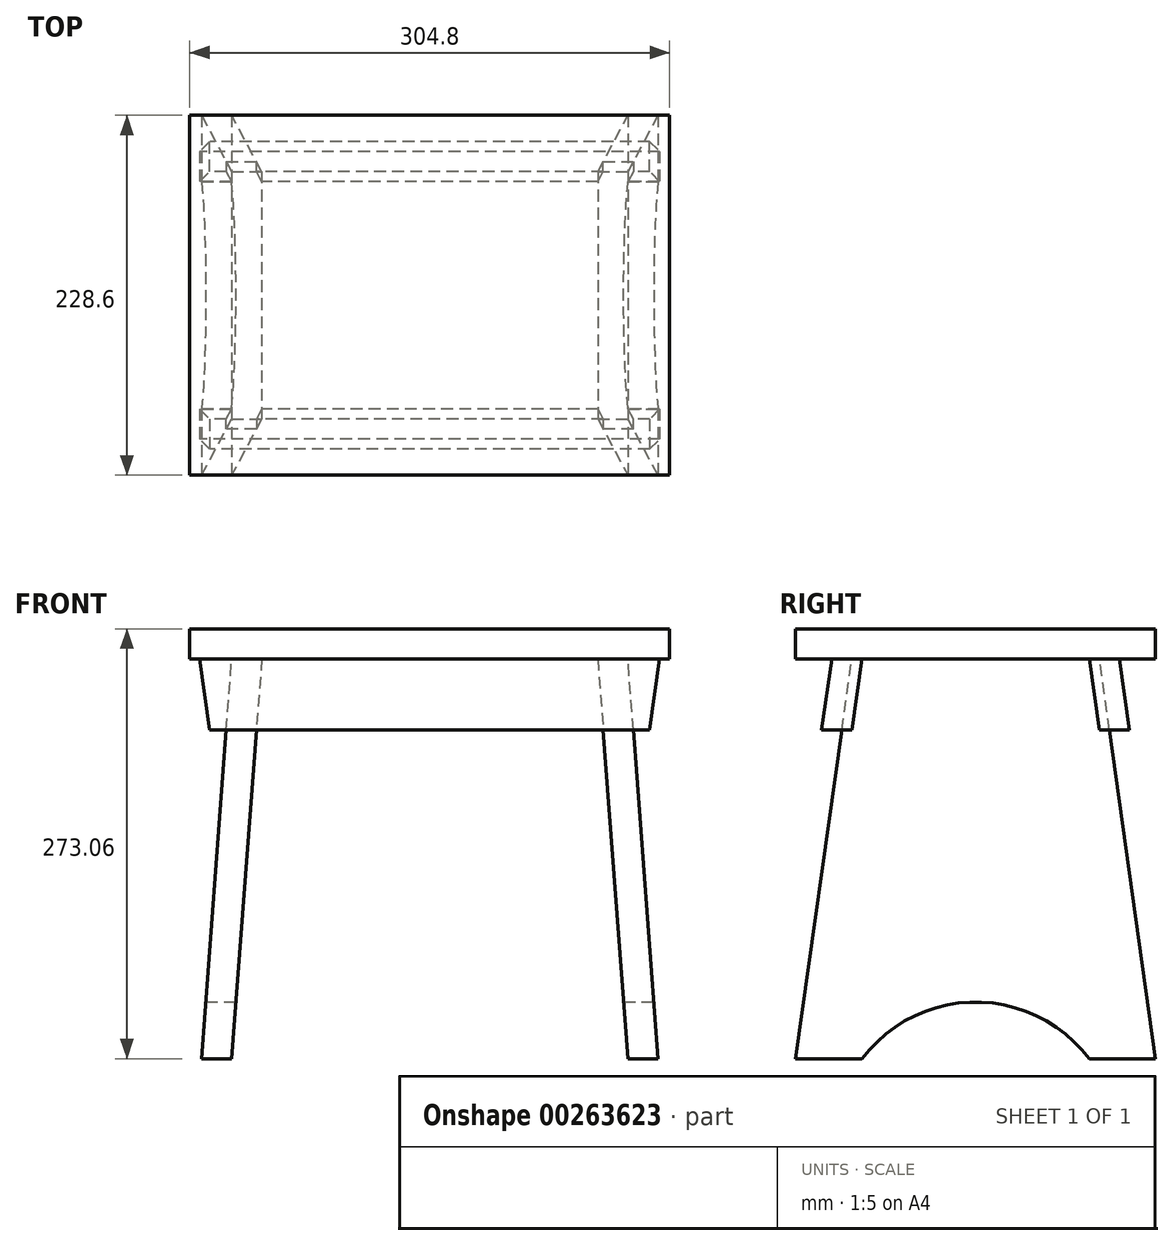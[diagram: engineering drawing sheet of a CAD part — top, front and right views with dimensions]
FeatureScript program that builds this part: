
annotation { "Feature Type Name" : "Feature", "Feature Type Description" : "" }
export const myFeature = defineFeature(function(context is Context, id is Id, definition is map)
    precondition{}
    {
        {
            var Q0;
            Q0=qCreatedBy(makeId("Front.planeOp"),FACE);
            var sketch = newSketch(context, id + "F0", { "sketchPlane" : qUnion([Q0])});
            skLineSegment(sketch, "E0.bottom", {"start": v(152.4, 9.52) * mm, "end": v(-152.4, 9.52) * mm});
            skLineSegment(sketch, "E0.top", {"start": v(152.4, -9.53) * mm, "end": v(-152.4, -9.53) * mm});
            skLineSegment(sketch, "E0.left", {"start": v(152.4, 9.52) * mm, "end": v(152.4, -9.52) * mm});
            skLineSegment(sketch, "E0.right", {"start": v(-152.4, 9.52) * mm, "end": v(-152.4, -9.53) * mm});
            skPoint(sketch, "E0.middle", {"position": v(0, 0) * mm});
            skLineSegment(sketch, "E1.bottom", {"start": v(-152.4, -9.53) * mm, "end": v(152.4, -9.53) * mm, "construction": true});
            skLineSegment(sketch, "E1.top", {"start": v(-152.4, -263.53) * mm, "end": v(152.4, -263.53) * mm, "construction": true});
            skLineSegment(sketch, "E1.left", {"start": v(-152.4, -9.52) * mm, "end": v(-152.4, -263.53) * mm, "construction": true});
            skLineSegment(sketch, "E1.right", {"start": v(152.4, -9.52) * mm, "end": v(152.4, -263.52) * mm, "construction": true});
            skLineSegment(sketch, "E2", {"start": v(106.74, -9.53) * mm, "end": v(125.85, -263.53) * mm});
            skLineSegment(sketch, "E3", {"start": v(125.85, -263.53) * mm, "end": v(144.95, -263.53) * mm});
            skLineSegment(sketch, "E4", {"start": v(144.95, -263.52) * mm, "end": v(125.85, -9.52) * mm});
            skLineSegment(sketch, "E5", {"start": v(125.85, -9.52) * mm, "end": v(106.74, -9.53) * mm});
            skLineSegment(sketch, "E6", {"start": v(0, -9.52) * mm, "end": v(0, -263.53) * mm, "construction": true});
            skLineSegment(sketch, "E7.MirrorCS", {"start": v(-144.95, -263.53) * mm, "end": v(-125.85, -9.52) * mm});
            skLineSegment(sketch, "E8.MirrorCS", {"start": v(-106.74, -9.52) * mm, "end": v(-125.85, -263.53) * mm});
            skLineSegment(sketch, "E9.MirrorCS", {"start": v(-125.85, -263.53) * mm, "end": v(-144.95, -263.53) * mm});
            skLineSegment(sketch, "E10.MirrorCS", {"start": v(-125.85, -9.52) * mm, "end": v(-106.74, -9.53) * mm});
            skLineSegment(sketch, "E11.bottom", {"start": v(-152.4, -9.53) * mm, "end": v(152.4, -9.53) * mm});
            skLineSegment(sketch, "E11.top", {"start": v(-152.4, -63.28) * mm, "end": v(152.4, -63.28) * mm});
            skLineSegment(sketch, "E11.left", {"start": v(-152.4, -9.53) * mm, "end": v(-152.4, -63.28) * mm});
            skLineSegment(sketch, "E11.right", {"start": v(152.4, -9.53) * mm, "end": v(152.4, -63.28) * mm});
            skLineSegment(sketch, "E12", {"start": v(146.05, -9.52) * mm, "end": v(138.5, -63.28) * mm});
            skLineSegment(sketch, "E13.MirrorCS", {"start": v(-146.05, -9.53) * mm, "end": v(-138.5, -63.28) * mm});
            skSolve(sketch);
        }
        {
            var Q0;
            Q0=makeQuery(id+"F0.imprint","IMPRINT",FACE,{"disambiguationData":[TD([[makeQuery(id+"F0.imprint","IMPRINT",EDGE,{"derivedFrom":sQuery(id+"F0.wireOp",EDGE,"E0.bottom")}),1.0]])]});
            extrude(context, id + "F1", {"entities" : qUnion([Q0]), "endBound" : BoundingType.SYMMETRIC, "depth" : 228.6 * mm});
        }
        {
            var Q0;
            {var subQ0=sQuery(id+"F0.wireOp",EDGE,"E3");Q0=makeQuery(id+"F0.imprint","IMPRINT",FACE,{"disambiguationData":[TD([[makeQuery(id+"F0.imprint","IMPRINT",EDGE,{"derivedFrom":subQ0}),1.0]])]});}
            var Q1;
            {var subQ0=sQuery(id+"F0.wireOp",EDGE,"E11.bottom");var subQ1=sQuery(id+"F0.wireOp",EDGE,"E2");var subQ2=makeQuery(id+"F0.imprint","INTERSECT",VERTEX,{"derivedFrom":[subQ1,subQ0]});Q1=makeQuery(id+"F0.imprint","IMPRINT",FACE,{"disambiguationData":[TD([[makeQuery(id+"F0.imprint","IMPRINT",EDGE,{"disambiguationData":[TD([[subQ2,-1.0]])],"derivedFrom":subQ1}),1.0]])]});}
            var Q2;
            {var subQ0=sQuery(id+"F0.wireOp",EDGE,"E11.bottom");var subQ1=sQuery(id+"F0.wireOp",EDGE,"E7.MirrorCS");var subQ2=makeQuery(id+"F0.imprint","INTERSECT",VERTEX,{"derivedFrom":[subQ1,subQ0]});Q2=makeQuery(id+"F0.imprint","IMPRINT",FACE,{"disambiguationData":[TD([[makeQuery(id+"F0.imprint","IMPRINT",EDGE,{"disambiguationData":[TD([[subQ2,1.0]])],"derivedFrom":subQ1}),-1.0]])]});}
            var Q3;
            {var subQ0=sQuery(id+"F0.wireOp",EDGE,"E9.MirrorCS");Q3=makeQuery(id+"F0.imprint","IMPRINT",FACE,{"disambiguationData":[TD([[makeQuery(id+"F0.imprint","IMPRINT",EDGE,{"derivedFrom":subQ0}),-1.0]])]});}
            var Q4;
            Q4=makeQuery(id+"F1.opExtrude","CAP_VERTEX",VERTEX,{"disambiguationData":[OSD([sQuery(id+"F0.wireOp",EDGE,"E0.right"),sQuery(id+"F0.wireOp",EDGE,"E11.bottom"),sQuery(id+"F0.wireOp",EDGE,"E11.left")])],"isStart":true});
            var Q5;
            Q5=makeQuery(id+"F1.opExtrude","CAP_VERTEX",VERTEX,{"disambiguationData":[OSD([sQuery(id+"F0.wireOp",EDGE,"E0.right"),sQuery(id+"F0.wireOp",EDGE,"E11.bottom"),sQuery(id+"F0.wireOp",EDGE,"E11.left")])],"isStart":false});
            extrude(context, id + "F2", {"entities" : qUnion([Q0, Q1, Q2, Q3]), "endBound" : BoundingType.UP_TO_VERTEX, "oppositeDirection" : true, "endBoundEntityVertex" : qUnion([Q4]), "depth" : 25.4 * mm, "hasSecondDirection" : true, "secondDirectionBound" : SecondDirectionBoundingType.UP_TO_VERTEX, "secondDirectionOppositeDirection" : false, "secondDirectionBoundEntityVertex" : qUnion([Q5]), "secondDirectionDepth" : 25.4 * mm});
        }
        {
            var Q0;
            Q0=qCreatedBy(makeId("Right.planeOp"),FACE);
            var sketch = newSketch(context, id + "F3", { "sketchPlane" : qUnion([Q0])});
            skLineSegment(sketch, "E14.0.0", {"start": v(-114.3, -263.53) * mm, "end": v(114.3, -263.53) * mm});
            skLineSegment(sketch, "E14.0.1", {"start": v(114.3, -263.53) * mm, "end": v(114.3, -9.53) * mm});
            skLineSegment(sketch, "E14.0.2", {"start": v(114.3, -9.53) * mm, "end": v(-114.3, -9.53) * mm});
            skLineSegment(sketch, "E14.0.3", {"start": v(-114.3, -9.53) * mm, "end": v(-114.3, -263.53) * mm});
            skLineSegment(sketch, "E15", {"start": v(114.3, -263.53) * mm, "end": v(78.6, -9.52) * mm});
            skLineSegment(sketch, "E16.MirrorCS", {"start": v(-114.3, -263.53) * mm, "end": v(-78.6, -9.52) * mm});
            skArc(sketch, "E17", {"start": v(72.12, -263.53) * mm, "mid": v(0, -227.49) * mm, "end": v(-72.12, -263.53) * mm});
            skLineSegment(sketch, "E18", {"start": v(0, -317.67) * mm, "end": v(0, -263.53) * mm, "construction": true});
            skSolve(sketch);
        }
        {
            var Q0;
            {var subQ0=sQuery(id+"F3.wireOp",EDGE,"E14.0.1");Q0=makeQuery(id+"F3.imprint","IMPRINT",FACE,{"disambiguationData":[TD([[makeQuery(id+"F3.imprint","IMPRINT",EDGE,{"derivedFrom":subQ0}),1.0]])]});}
            var Q1;
            {var subQ0=sQuery(id+"F3.wireOp",EDGE,"E17");Q1=makeQuery(id+"F3.imprint","IMPRINT",FACE,{"disambiguationData":[TD([[makeQuery(id+"F3.imprint","IMPRINT",EDGE,{"derivedFrom":subQ0}),1.0]])]});}
            var Q2;
            {var subQ0=sQuery(id+"F3.wireOp",EDGE,"E14.0.3");Q2=makeQuery(id+"F3.imprint","IMPRINT",FACE,{"disambiguationData":[TD([[makeQuery(id+"F3.imprint","IMPRINT",EDGE,{"derivedFrom":subQ0}),1.0]])]});}
            extrude(context, id + "F4", {"entities" : qUnion([Q0, Q1, Q2]), "operationType" : NewBodyOperationType.REMOVE, "endBound" : BoundingType.THROUGH_ALL, "oppositeDirection" : true, "depth" : 25.4 * mm, "hasSecondDirection" : true, "secondDirectionBound" : SecondDirectionBoundingType.THROUGH_ALL, "secondDirectionOppositeDirection" : false, "secondDirectionDepth" : 25.4 * mm});
        }
        {
            var Q0;
            Q0=qCreatedBy(makeId("Right.planeOp"),FACE);
            var sketch = newSketch(context, id + "F5", { "sketchPlane" : qUnion([Q0])});
            skLineSegment(sketch, "E19.0.0", {"start": v(78.6, -9.52) * mm, "end": v(114.3, -263.53) * mm});
            skLineSegment(sketch, "E19.0.1", {"start": v(114.3, -263.53) * mm, "end": v(72.12, -263.53) * mm});
            skArc(sketch, "E19.0.2", {"start": v(72.12, -263.53) * mm, "mid": v(0, -227.49) * mm, "end": v(-72.12, -263.52) * mm});
            skLineSegment(sketch, "E19.0.3", {"start": v(-72.12, -263.53) * mm, "end": v(-114.3, -263.53) * mm});
            skLineSegment(sketch, "E19.0.4", {"start": v(-114.3, -263.52) * mm, "end": v(-78.6, -9.52) * mm});
            skLineSegment(sketch, "E19.0.5", {"start": v(-78.6, -9.53) * mm, "end": v(78.6, -9.53) * mm});
            skLineSegment(sketch, "E20", {"start": v(-91.43, -9.52) * mm, "end": v(-97.79, -54.77) * mm});
            skLineSegment(sketch, "E21", {"start": v(-97.79, -54.77) * mm, "end": v(-78.55, -54.77) * mm});
            skLineSegment(sketch, "E22", {"start": v(-78.55, -54.77) * mm, "end": v(-72.2, -9.52) * mm});
            skLineSegment(sketch, "E23", {"start": v(-72.2, -9.53) * mm, "end": v(-91.43, -9.53) * mm});
            skLineSegment(sketch, "E24.MirrorCS", {"start": v(114.3, -263.52) * mm, "end": v(78.6, -9.52) * mm});
            skLineSegment(sketch, "E25.MirrorCS", {"start": v(78.55, -54.77) * mm, "end": v(72.2, -9.52) * mm});
            skLineSegment(sketch, "E26.MirrorCS", {"start": v(97.79, -54.77) * mm, "end": v(78.55, -54.77) * mm});
            skLineSegment(sketch, "E27.MirrorCS", {"start": v(91.43, -9.52) * mm, "end": v(97.79, -54.77) * mm});
            skLineSegment(sketch, "E28.MirrorCS", {"start": v(72.2, -9.52) * mm, "end": v(91.43, -9.52) * mm});
            skSolve(sketch);
        }
        {
            var Q0;
            {var subQ5=sQuery(id+"F5.wireOp",EDGE,"E25.MirrorCS");Q0=makeQuery(id+"F5.imprint","IMPRINT",FACE,{"disambiguationData":[TD([[makeQuery(id+"F5.imprint","IMPRINT",EDGE,{"derivedFrom":subQ5}),-1.0]])]});}
            var Q1;
            {var subQ5=sQuery(id+"F5.wireOp",EDGE,"E27.MirrorCS");Q1=makeQuery(id+"F5.imprint","IMPRINT",FACE,{"disambiguationData":[TD([[makeQuery(id+"F5.imprint","IMPRINT",EDGE,{"derivedFrom":subQ5}),-1.0]])]});}
            var Q2;
            {var subQ5=sQuery(id+"F5.wireOp",EDGE,"E22");Q2=makeQuery(id+"F5.imprint","IMPRINT",FACE,{"disambiguationData":[TD([[makeQuery(id+"F5.imprint","IMPRINT",EDGE,{"derivedFrom":subQ5}),1.0]])]});}
            var Q3;
            {var subQ5=sQuery(id+"F5.wireOp",EDGE,"E20");Q3=makeQuery(id+"F5.imprint","IMPRINT",FACE,{"disambiguationData":[TD([[makeQuery(id+"F5.imprint","IMPRINT",EDGE,{"derivedFrom":subQ5}),1.0]])]});}
            var Q4;
            Q4=makeQuery(id+"F1.opExtrude","SWEPT_FACE",FACE,{"disambiguationData":[OSD([sQuery(id+"F0.wireOp",EDGE,"E0.left")])]});
            var Q5;
            Q5=makeQuery(id+"F1.opExtrude","SWEPT_FACE",FACE,{"disambiguationData":[OSD([sQuery(id+"F0.wireOp",EDGE,"E0.right")])]});
            extrude(context, id + "F6", {"entities" : qUnion([Q0, Q1, Q2, Q3]), "endBound" : BoundingType.UP_TO_SURFACE, "endBoundEntityFace" : qUnion([Q4]), "depth" : 25.4 * mm, "hasSecondDirection" : true, "secondDirectionBound" : SecondDirectionBoundingType.UP_TO_SURFACE, "secondDirectionOppositeDirection" : true, "secondDirectionBoundEntityFace" : qUnion([Q5]), "secondDirectionDepth" : 25.4 * mm});
        }
        {
            var Q0;
            {var subQ0=sQuery(id+"F0.wireOp",EDGE,"E11.left");Q0=makeQuery(id+"F0.imprint","IMPRINT",FACE,{"disambiguationData":[TD([[makeQuery(id+"F0.imprint","IMPRINT",EDGE,{"derivedFrom":subQ0}),1.0]])]});}
            var Q1;
            {var subQ0=sQuery(id+"F0.wireOp",EDGE,"E11.right");Q1=makeQuery(id+"F0.imprint","IMPRINT",FACE,{"disambiguationData":[TD([[makeQuery(id+"F0.imprint","IMPRINT",EDGE,{"derivedFrom":subQ0}),-1.0]])]});}
            extrude(context, id + "F7", {"entities" : qUnion([Q0, Q1]), "operationType" : NewBodyOperationType.REMOVE, "endBound" : BoundingType.THROUGH_ALL, "oppositeDirection" : true, "depth" : 25.4 * mm, "hasSecondDirection" : true, "secondDirectionBound" : SecondDirectionBoundingType.THROUGH_ALL, "secondDirectionOppositeDirection" : false, "secondDirectionDepth" : 25.4 * mm});
        }
        {
            var Q0;
            Q0=makeQuery(id+"F2.opExtrude","SWEPT_BODY",BODY,{"disambiguationData":[OSD([sQuery(id+"F0.wireOp",EDGE,"E7.MirrorCS"),sQuery(id+"F0.wireOp",EDGE,"E8.MirrorCS"),sQuery(id+"F0.wireOp",EDGE,"E9.MirrorCS"),sQuery(id+"F0.wireOp",EDGE,"E11.bottom")])]});
            var Q1;
            Q1=makeQuery(id+"F6.opExtrude","SWEPT_BODY",BODY,{"disambiguationData":[OSD([sQuery(id+"F5.wireOp",EDGE,"E28.MirrorCS"),sQuery(id+"F5.wireOp",EDGE,"E26.MirrorCS"),sQuery(id+"F5.wireOp",EDGE,"E25.MirrorCS"),sQuery(id+"F5.wireOp",EDGE,"E27.MirrorCS")])]});
            booleanBodies(context, id + "F8", {"operationType" : BooleanOperationType.SUBTRACTION, "tools" : qUnion([Q0]), "targets" : qUnion([Q1]), "keepTools" : true});
        }
        {
            var Q0;
            Q0=makeQuery(id+"F2.opExtrude","SWEPT_BODY",BODY,{"disambiguationData":[OSD([sQuery(id+"F0.wireOp",EDGE,"E2"),sQuery(id+"F0.wireOp",EDGE,"E3"),sQuery(id+"F0.wireOp",EDGE,"E4"),sQuery(id+"F0.wireOp",EDGE,"E11.bottom")])]});
            var Q1;
            Q1=makeQuery(id+"F6.opExtrude","SWEPT_BODY",BODY,{"disambiguationData":[OSD([sQuery(id+"F5.wireOp",EDGE,"E28.MirrorCS"),sQuery(id+"F5.wireOp",EDGE,"E26.MirrorCS"),sQuery(id+"F5.wireOp",EDGE,"E25.MirrorCS"),sQuery(id+"F5.wireOp",EDGE,"E27.MirrorCS")])]});
            booleanBodies(context, id + "F9", {"operationType" : BooleanOperationType.SUBTRACTION, "tools" : qUnion([Q0]), "targets" : qUnion([Q1]), "keepTools" : true});
        }
        {
            var Q0;
            Q0=makeQuery(id+"F2.opExtrude","SWEPT_BODY",BODY,{"disambiguationData":[OSD([sQuery(id+"F0.wireOp",EDGE,"E2"),sQuery(id+"F0.wireOp",EDGE,"E3"),sQuery(id+"F0.wireOp",EDGE,"E4"),sQuery(id+"F0.wireOp",EDGE,"E11.bottom")])]});
            var Q1;
            Q1=makeQuery(id+"F6.opExtrude","SWEPT_BODY",BODY,{"disambiguationData":[OSD([sQuery(id+"F5.wireOp",EDGE,"E20"),sQuery(id+"F5.wireOp",EDGE,"E21"),sQuery(id+"F5.wireOp",EDGE,"E22"),sQuery(id+"F5.wireOp",EDGE,"E23")])]});
            booleanBodies(context, id + "F10", {"operationType" : BooleanOperationType.SUBTRACTION, "tools" : qUnion([Q0]), "targets" : qUnion([Q1]), "keepTools" : true});
        }
        {
            var Q0;
            Q0=makeQuery(id+"F2.opExtrude","SWEPT_BODY",BODY,{"disambiguationData":[OSD([sQuery(id+"F0.wireOp",EDGE,"E7.MirrorCS"),sQuery(id+"F0.wireOp",EDGE,"E8.MirrorCS"),sQuery(id+"F0.wireOp",EDGE,"E9.MirrorCS"),sQuery(id+"F0.wireOp",EDGE,"E11.bottom")])]});
            var Q1;
            Q1=makeQuery(id+"F6.opExtrude","SWEPT_BODY",BODY,{"disambiguationData":[OSD([sQuery(id+"F5.wireOp",EDGE,"E20"),sQuery(id+"F5.wireOp",EDGE,"E21"),sQuery(id+"F5.wireOp",EDGE,"E22"),sQuery(id+"F5.wireOp",EDGE,"E23")])]});
            booleanBodies(context, id + "F11", {"operationType" : BooleanOperationType.SUBTRACTION, "tools" : qUnion([Q0]), "targets" : qUnion([Q1]), "keepTools" : true});
        }
    });
